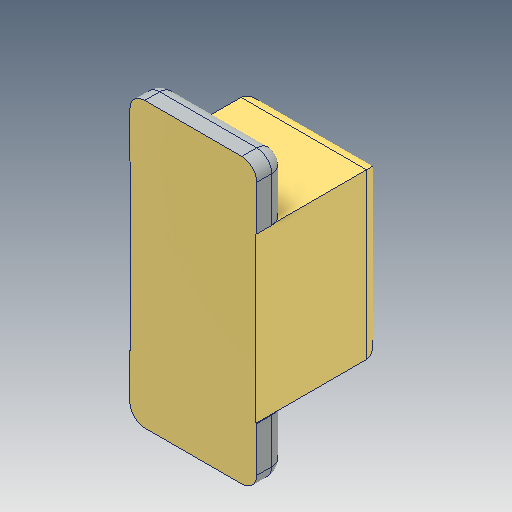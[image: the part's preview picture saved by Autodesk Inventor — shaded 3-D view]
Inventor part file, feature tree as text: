
AUTODESK INVENTOR PART (.ipt)
format: ipt  version: 2018 (Build 220112000, 112)  size: 120,320 bytes
history: native  units: mm
features: fillet x1
ambient origin geometry x8: Origin, YZ Plane, XZ Plane, XY Plane, X Axis, Y Axis, Z Axis, Center Point
bodies: Volumenkörper1 (feature_tree)
feature tree (1):
  fillet  "Fillet3"  [1 undecoded]
note: 1 required parameter value undecoded (feature->parameter linkage not recoverable at this tier; creation-order binding heuristic only, values carry confidence <= 0.55)
